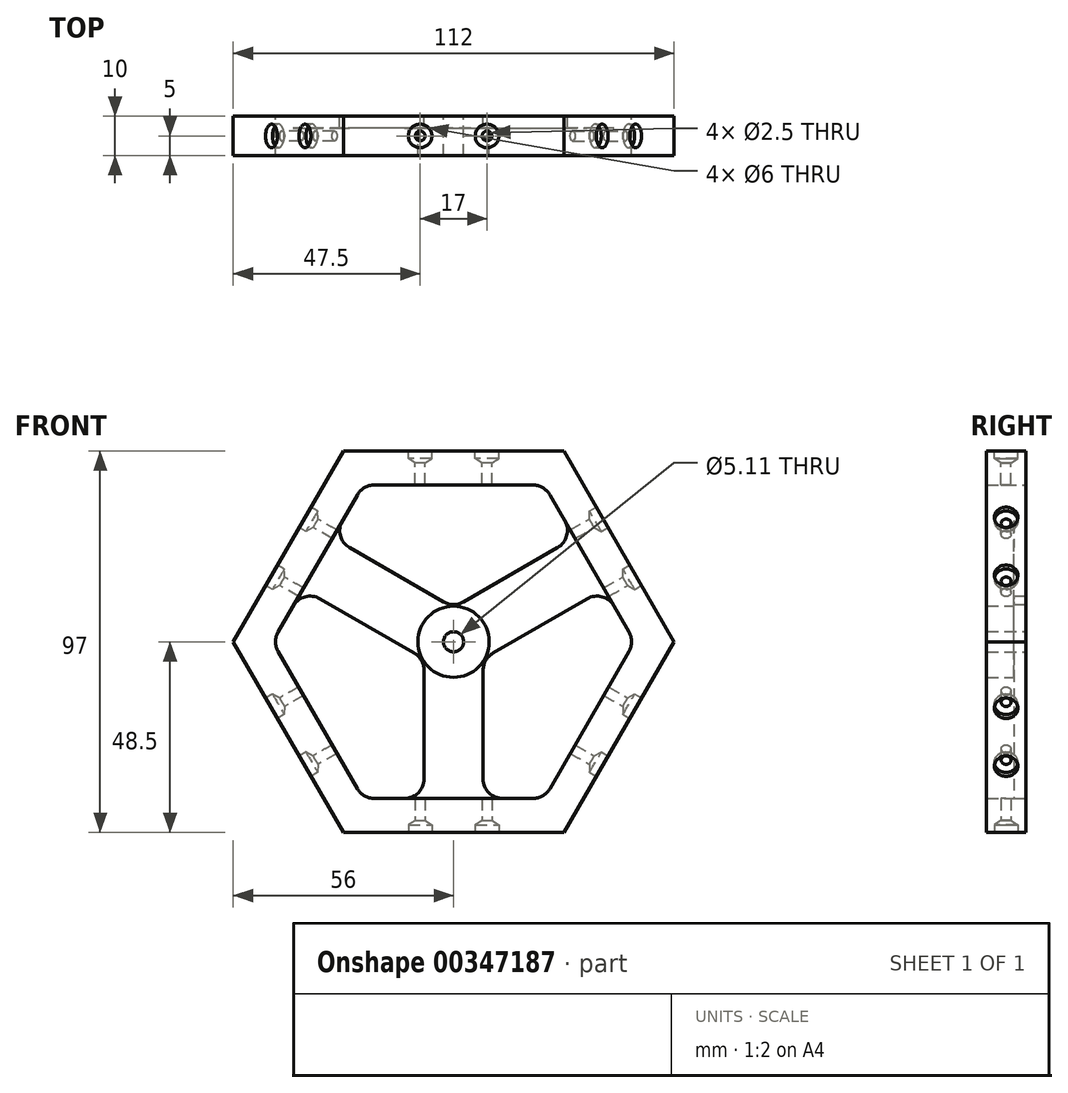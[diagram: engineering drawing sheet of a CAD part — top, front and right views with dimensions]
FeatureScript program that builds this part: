
annotation { "Feature Type Name" : "Feature", "Feature Type Description" : "" }
export const myFeature = defineFeature(function(context is Context, id is Id, definition is map)
    precondition{}
    {
        {
            var Q0;
            Q0=qCreatedBy(makeId("Front.planeOp"),FACE);
            var sketch = newSketch(context, id + "F0", { "sketchPlane" : qUnion([Q0])});
            skCircle(sketch, "E0.cCircle", {"center": v(0, 0) * mm, "radius": 56 * mm, "construction": true});
            skLineSegment(sketch, "E0.0", {"start": v(56, 0) * mm, "end": v(28, -48.5) * mm});
            skLineSegment(sketch, "E0.1", {"start": v(28, -48.5) * mm, "end": v(-28, -48.5) * mm});
            skLineSegment(sketch, "E0.2", {"start": v(-28, -48.5) * mm, "end": v(-56, 0) * mm});
            skLineSegment(sketch, "E0.3", {"start": v(-56, 0) * mm, "end": v(-28, 48.5) * mm});
            skLineSegment(sketch, "E0.4", {"start": v(-28, 48.5) * mm, "end": v(28, 48.5) * mm});
            skLineSegment(sketch, "E0.5", {"start": v(28, 48.5) * mm, "end": v(56, 0) * mm});
            skCircle(sketch, "E1.cCircle", {"center": v(0, 0) * mm, "radius": 46 * mm, "construction": true});
            skLineSegment(sketch, "E1.0", {"start": v(44.56, -2.5) * mm, "end": v(24.44, -37.34) * mm});
            skLineSegment(sketch, "E1.1", {"start": v(20.11, -39.84) * mm, "end": v(12.5, -39.84) * mm});
            skLineSegment(sketch, "E1.2", {"start": v(-24.44, -37.34) * mm, "end": v(-44.56, -2.5) * mm});
            skLineSegment(sketch, "E1.3", {"start": v(-28.25, 30.74) * mm, "end": v(-24.44, 37.34) * mm});
            skLineSegment(sketch, "E1.4", {"start": v(-20.11, 39.84) * mm, "end": v(20.11, 39.84) * mm});
            skLineSegment(sketch, "E1.5", {"start": v(24.44, 37.34) * mm, "end": v(28.25, 30.74) * mm});
            skLineSegment(sketch, "E2", {"start": v(7.5, -7.22) * mm, "end": v(7.5, -34.84) * mm});
            skLineSegment(sketch, "E3", {"start": v(-7.5, -7.22) * mm, "end": v(-7.5, -34.84) * mm});
            skLineSegment(sketch, "E4", {"start": v(10, -2.89) * mm, "end": v(33.92, 10.92) * mm});
            skLineSegment(sketch, "E5", {"start": v(2.5, 10.1) * mm, "end": v(26.42, 23.91) * mm});
            skLineSegment(sketch, "E6", {"start": v(-2.5, 10.1) * mm, "end": v(-26.42, 23.91) * mm});
            skLineSegment(sketch, "E7", {"start": v(-10, -2.89) * mm, "end": v(-33.92, 10.92) * mm});
            skPoint(sketch, "E8.newPointB", {"position": v(-46, 0) * mm});
            skArc(sketch, "E8.filletArc", {"start": v(-28.25, 30.74) * mm, "mid": v(-28.75, 26.95) * mm, "end": v(-26.42, 23.91) * mm});
            skPoint(sketch, "E9.visualSharp", {"position": v(-23, 39.84) * mm});
            skArc(sketch, "E9.filletArc", {"start": v(-20.11, 39.84) * mm, "mid": v(-22.61, 39.17) * mm, "end": v(-24.44, 37.34) * mm});
            skPoint(sketch, "E10.visualSharp", {"position": v(23, 39.84) * mm});
            skArc(sketch, "E10.filletArc", {"start": v(24.44, 37.34) * mm, "mid": v(22.61, 39.17) * mm, "end": v(20.11, 39.84) * mm});
            skPoint(sketch, "E11.newPointA", {"position": v(46, 0) * mm});
            skArc(sketch, "E11.filletArc", {"start": v(26.42, 23.91) * mm, "mid": v(28.75, 26.95) * mm, "end": v(28.25, 30.74) * mm});
            skPoint(sketch, "E12.visualSharp", {"position": v(23, -39.84) * mm});
            skArc(sketch, "E12.filletArc", {"start": v(20.11, -39.84) * mm, "mid": v(22.61, -39.17) * mm, "end": v(24.44, -37.34) * mm});
            skArc(sketch, "E13.filletArc", {"start": v(7.5, -34.84) * mm, "mid": v(8.96, -38.37) * mm, "end": v(12.5, -39.84) * mm});
            skArc(sketch, "E14.filletArc", {"start": v(10, -2.89) * mm, "mid": v(8.17, -4.72) * mm, "end": v(7.5, -7.22) * mm});
            skArc(sketch, "E15.filletArc", {"start": v(-7.5, -7.22) * mm, "mid": v(-8.17, -4.72) * mm, "end": v(-10, -2.89) * mm});
            skArc(sketch, "E16.filletArc", {"start": v(-2.5, 10.1) * mm, "mid": v(0, 9.43) * mm, "end": v(2.5, 10.1) * mm});
            skLineSegment(sketch, "E17", {"start": v(-40.75, 9.1) * mm, "end": v(-44.56, 2.5) * mm});
            skLineSegment(sketch, "E18", {"start": v(-20.11, -39.84) * mm, "end": v(-12.5, -39.84) * mm});
            skLineSegment(sketch, "E19", {"start": v(44.56, 2.5) * mm, "end": v(40.75, 9.1) * mm});
            skPoint(sketch, "E20.visualSharp", {"position": v(38.25, 13.42) * mm});
            skArc(sketch, "E20.filletArc", {"start": v(40.75, 9.1) * mm, "mid": v(37.71, 11.42) * mm, "end": v(33.92, 10.92) * mm});
            skArc(sketch, "E21.filletArc", {"start": v(44.56, -2.5) * mm, "mid": v(45.23, 0) * mm, "end": v(44.56, 2.5) * mm});
            skPoint(sketch, "E22.visualSharp", {"position": v(-38.25, 13.42) * mm});
            skArc(sketch, "E22.filletArc", {"start": v(-33.92, 10.92) * mm, "mid": v(-37.71, 11.42) * mm, "end": v(-40.75, 9.1) * mm});
            skPoint(sketch, "E23.visualSharp", {"position": v(-7.5, -39.84) * mm});
            skArc(sketch, "E23.filletArc", {"start": v(-12.5, -39.84) * mm, "mid": v(-8.96, -38.37) * mm, "end": v(-7.5, -34.84) * mm});
            skPoint(sketch, "E24.visualSharp", {"position": v(-23, -39.84) * mm});
            skArc(sketch, "E24.filletArc", {"start": v(-24.44, -37.34) * mm, "mid": v(-22.61, -39.17) * mm, "end": v(-20.11, -39.84) * mm});
            skArc(sketch, "E25.filletArc", {"start": v(-44.56, 2.5) * mm, "mid": v(-45.23, 0) * mm, "end": v(-44.56, -2.5) * mm});
            skCircle(sketch, "E26", {"center": v(0, 0) * mm, "radius": 9.05 * mm});
            skLineSegment(sketch, "E27", {"start": v(-28.25, 30.74) * mm, "end": v(-40.75, 9.1) * mm});
            skLineSegment(sketch, "E28", {"start": v(28.25, 30.74) * mm, "end": v(40.75, 9.1) * mm});
            skLineSegment(sketch, "E29", {"start": v(12.5, -39.84) * mm, "end": v(-12.5, -39.84) * mm});
            skSolve(sketch);
        }
        {
            var Q0;
            Q0=makeQuery(id+"F0.imprint","IMPRINT",FACE,{"disambiguationData":[TD([[makeQuery(id+"F0.imprint","IMPRINT",EDGE,{"derivedFrom":sQuery(id+"F0.wireOp",EDGE,"E0.0")}),-1.0]])]});
            var Q1;
            Q1=makeQuery(id+"F0.imprint","IMPRINT",FACE,{"disambiguationData":[TD([[makeQuery(id+"F0.imprint","IMPRINT",EDGE,{"derivedFrom":sQuery(id+"F0.wireOp",EDGE,"E26")}),1.0]])]});
            var Q2;
            Q2=makeQuery(id+"F0.imprint","IMPRINT",FACE,{"disambiguationData":[TD([[makeQuery(id+"F0.imprint","IMPRINT",EDGE,{"derivedFrom":sQuery(id+"F0.wireOp",EDGE,"E2")}),-1.0]])]});
            extrude(context, id + "F1", {"entities" : qUnion([Q0, Q1, Q2]), "depth" : 3 * mm});
        }
        {
            var Q0;
            Q0 = qSketchRegion(id + "F0", true);
            var Q1;
            Q1=makeQuery(id+"F0.imprint","IMPRINT",FACE,{"disambiguationData":[TD([[makeQuery(id+"F0.imprint","IMPRINT",EDGE,{"derivedFrom":sQuery(id+"F0.wireOp",EDGE,"E26")}),1.0]])]});
            extrude(context, id + "F2", {"entities" : qUnion([Q0, Q1]), "operationType" : NewBodyOperationType.ADD, "depth" : 10 * mm});
        }
        {
            var Q0;
            {var subQ0=sQuery(id+"F0.wireOp",EDGE,"E0.1");Q0=makeQuery(id+"F2.boolean.opBoolean","MERGE",FACE,{"derivedFrom":[makeQuery(id+"F1.opExtrude","SWEPT_FACE",FACE,{"disambiguationData":[OSD([subQ0])]}),makeQuery(id+"F2.opExtrude","SWEPT_FACE",FACE,{"disambiguationData":[OSD([subQ0])]})]});}
            var sketch = newSketch(context, id + "F3", { "sketchPlane" : qUnion([Q0])});
            skPoint(sketch, "E30", {"position": v(-8.5, 5) * mm});
            skPoint(sketch, "E31", {"position": v(8.5, 5) * mm});
            skSolve(sketch);
        }
        {
            var Q0;
            {var subQ0=sQuery(id+"F0.wireOp",EDGE,"E0.0");Q0=makeQuery(id+"F2.boolean.opBoolean","MERGE",FACE,{"derivedFrom":[makeQuery(id+"F1.opExtrude","SWEPT_FACE",FACE,{"disambiguationData":[OSD([subQ0])]}),makeQuery(id+"F2.opExtrude","SWEPT_FACE",FACE,{"disambiguationData":[OSD([subQ0])]})]});}
            var sketch = newSketch(context, id + "F4", { "sketchPlane" : qUnion([Q0])});
            skPoint(sketch, "E32", {"position": v(-5, -8.5) * mm});
            skPoint(sketch, "E33", {"position": v(-5, 8.5) * mm});
            skSolve(sketch);
        }
        {
            var Q0;
            {var subQ0=sQuery(id+"F0.wireOp",EDGE,"E0.5");Q0=makeQuery(id+"F2.boolean.opBoolean","MERGE",FACE,{"derivedFrom":[makeQuery(id+"F1.opExtrude","SWEPT_FACE",FACE,{"disambiguationData":[OSD([subQ0])]}),makeQuery(id+"F2.opExtrude","SWEPT_FACE",FACE,{"disambiguationData":[OSD([subQ0])]})]});}
            var sketch = newSketch(context, id + "F5", { "sketchPlane" : qUnion([Q0])});
            skPoint(sketch, "E34", {"position": v(-5, -8.5) * mm});
            skPoint(sketch, "E35", {"position": v(-5, 8.5) * mm});
            skSolve(sketch);
        }
        {
            var Q0;
            {var subQ0=sQuery(id+"F0.wireOp",EDGE,"E0.3");Q0=makeQuery(id+"F2.boolean.opBoolean","MERGE",FACE,{"derivedFrom":[makeQuery(id+"F1.opExtrude","SWEPT_FACE",FACE,{"disambiguationData":[OSD([subQ0])]}),makeQuery(id+"F2.opExtrude","SWEPT_FACE",FACE,{"disambiguationData":[OSD([subQ0])]})]});}
            var sketch = newSketch(context, id + "F6", { "sketchPlane" : qUnion([Q0])});
            skPoint(sketch, "E36.endSnap0", {"position": v(5, 28) * mm});
            skPoint(sketch, "E37", {"position": v(5, 8.5) * mm});
            skPoint(sketch, "E38", {"position": v(5, -8.5) * mm});
            skSolve(sketch);
        }
        {
            var Q0;
            {var subQ0=sQuery(id+"F0.wireOp",EDGE,"E0.2");Q0=makeQuery(id+"F2.boolean.opBoolean","MERGE",FACE,{"derivedFrom":[makeQuery(id+"F1.opExtrude","SWEPT_FACE",FACE,{"disambiguationData":[OSD([subQ0])]}),makeQuery(id+"F2.opExtrude","SWEPT_FACE",FACE,{"disambiguationData":[OSD([subQ0])]})]});}
            var sketch = newSketch(context, id + "F7", { "sketchPlane" : qUnion([Q0])});
            skPoint(sketch, "E39", {"position": v(5, 8.5) * mm});
            skPoint(sketch, "E40", {"position": v(5, -8.5) * mm});
            skSolve(sketch);
        }
        {
            var Q0;
            Q0=sQuery(id+"F3.wireOp",VERTEX,"E30");
            var Q1;
            Q1=sQuery(id+"F3.wireOp",VERTEX,"E31");
            var Q2;
            Q2=makeQuery(id+"F1.opExtrude","SWEPT_BODY",BODY,{"disambiguationData":[OSD([sQuery(id+"F0.wireOp",EDGE,"E0.0"),sQuery(id+"F0.wireOp",EDGE,"E0.1"),sQuery(id+"F0.wireOp",EDGE,"E0.2"),sQuery(id+"F0.wireOp",EDGE,"E0.3"),sQuery(id+"F0.wireOp",EDGE,"E0.4"),sQuery(id+"F0.wireOp",EDGE,"E0.5"),sQuery(id+"F0.wireOp",EDGE,"E1.0"),sQuery(id+"F0.wireOp",EDGE,"E1.1"),sQuery(id+"F0.wireOp",EDGE,"E1.2"),sQuery(id+"F0.wireOp",EDGE,"E1.3"),sQuery(id+"F0.wireOp",EDGE,"E1.4"),sQuery(id+"F0.wireOp",EDGE,"E1.5"),sQuery(id+"F0.wireOp",EDGE,"E2"),sQuery(id+"F0.wireOp",EDGE,"E3"),sQuery(id+"F0.wireOp",EDGE,"E4"),sQuery(id+"F0.wireOp",EDGE,"E5"),sQuery(id+"F0.wireOp",EDGE,"E6"),sQuery(id+"F0.wireOp",EDGE,"E7"),sQuery(id+"F0.wireOp",EDGE,"E8.filletArc"),sQuery(id+"F0.wireOp",EDGE,"E9.filletArc"),sQuery(id+"F0.wireOp",EDGE,"E10.filletArc"),sQuery(id+"F0.wireOp",EDGE,"E11.filletArc"),sQuery(id+"F0.wireOp",EDGE,"E12.filletArc"),sQuery(id+"F0.wireOp",EDGE,"E13.filletArc"),sQuery(id+"F0.wireOp",EDGE,"E14.filletArc"),sQuery(id+"F0.wireOp",EDGE,"E15.filletArc"),sQuery(id+"F0.wireOp",EDGE,"E16.filletArc"),sQuery(id+"F0.wireOp",EDGE,"E17"),sQuery(id+"F0.wireOp",EDGE,"E18"),sQuery(id+"F0.wireOp",EDGE,"E19"),sQuery(id+"F0.wireOp",EDGE,"E20.filletArc"),sQuery(id+"F0.wireOp",EDGE,"E21.filletArc"),sQuery(id+"F0.wireOp",EDGE,"E22.filletArc"),sQuery(id+"F0.wireOp",EDGE,"E23.filletArc"),sQuery(id+"F0.wireOp",EDGE,"E24.filletArc"),sQuery(id+"F0.wireOp",EDGE,"E25.filletArc")])]});
            hole(context, id + "F8", {"style" : HoleStyle.SIMPLE, "endStyle" : HoleEndStyle.BLIND, "holeDiameter" : 6 * mm, "holeDepth" : 2 * mm, "tappedDepth" : 12 * mm, "tapClearance" : 3, "locations" : qUnion([Q0, Q1]), "scope" : qUnion([Q2])});
        }
        {
            var Q0;
            Q0=sQuery(id+"F3.wireOp",VERTEX,"E30");
            var Q1;
            Q1=sQuery(id+"F3.wireOp",VERTEX,"E31");
            var Q2;
            Q2=makeQuery(id+"F1.opExtrude","SWEPT_BODY",BODY,{"disambiguationData":[OSD([sQuery(id+"F0.wireOp",EDGE,"E0.0"),sQuery(id+"F0.wireOp",EDGE,"E0.1"),sQuery(id+"F0.wireOp",EDGE,"E0.2"),sQuery(id+"F0.wireOp",EDGE,"E0.3"),sQuery(id+"F0.wireOp",EDGE,"E0.4"),sQuery(id+"F0.wireOp",EDGE,"E0.5"),sQuery(id+"F0.wireOp",EDGE,"E1.0"),sQuery(id+"F0.wireOp",EDGE,"E1.1"),sQuery(id+"F0.wireOp",EDGE,"E1.2"),sQuery(id+"F0.wireOp",EDGE,"E1.3"),sQuery(id+"F0.wireOp",EDGE,"E1.4"),sQuery(id+"F0.wireOp",EDGE,"E1.5"),sQuery(id+"F0.wireOp",EDGE,"E2"),sQuery(id+"F0.wireOp",EDGE,"E3"),sQuery(id+"F0.wireOp",EDGE,"E4"),sQuery(id+"F0.wireOp",EDGE,"E5"),sQuery(id+"F0.wireOp",EDGE,"E6"),sQuery(id+"F0.wireOp",EDGE,"E7"),sQuery(id+"F0.wireOp",EDGE,"E8.filletArc"),sQuery(id+"F0.wireOp",EDGE,"E9.filletArc"),sQuery(id+"F0.wireOp",EDGE,"E10.filletArc"),sQuery(id+"F0.wireOp",EDGE,"E11.filletArc"),sQuery(id+"F0.wireOp",EDGE,"E12.filletArc"),sQuery(id+"F0.wireOp",EDGE,"E13.filletArc"),sQuery(id+"F0.wireOp",EDGE,"E14.filletArc"),sQuery(id+"F0.wireOp",EDGE,"E15.filletArc"),sQuery(id+"F0.wireOp",EDGE,"E16.filletArc"),sQuery(id+"F0.wireOp",EDGE,"E17"),sQuery(id+"F0.wireOp",EDGE,"E18"),sQuery(id+"F0.wireOp",EDGE,"E19"),sQuery(id+"F0.wireOp",EDGE,"E20.filletArc"),sQuery(id+"F0.wireOp",EDGE,"E21.filletArc"),sQuery(id+"F0.wireOp",EDGE,"E22.filletArc"),sQuery(id+"F0.wireOp",EDGE,"E23.filletArc"),sQuery(id+"F0.wireOp",EDGE,"E24.filletArc"),sQuery(id+"F0.wireOp",EDGE,"E25.filletArc")])]});
            hole(context, id + "F9", {"style" : HoleStyle.SIMPLE, "endStyle" : HoleEndStyle.BLIND, "standardTappedOrClearance" : lookupTablePath({ "standard" : "ISO", "engagement" : "75%", "pitch" : "0.5 mm", "size" : "M3", "type" : "Tapped" }), "standardBlindInLast" : lookupTablePath({ "standard" : "ISO", "engagement" : "75%", "pitch" : "0.5 mm", "size" : "M3", "type" : "Tapped" }), "holeDiameter" : 2.5 * mm, "showTappedDepth" : true, "holeDepth" : 13.5 * mm, "tappedDepth" : 12 * mm, "tapClearance" : 3, "locations" : qUnion([Q0, Q1]), "scope" : qUnion([Q2]), "majorDiameter" : 3 * mm});
        }
        {
            var Q0;
            Q0=sQuery(id+"F4.wireOp",VERTEX,"E32");
            var Q1;
            Q1=sQuery(id+"F4.wireOp",VERTEX,"E33");
            var Q2;
            Q2=makeQuery(id+"F1.opExtrude","SWEPT_BODY",BODY,{"disambiguationData":[OSD([sQuery(id+"F0.wireOp",EDGE,"E0.0"),sQuery(id+"F0.wireOp",EDGE,"E0.1"),sQuery(id+"F0.wireOp",EDGE,"E0.2"),sQuery(id+"F0.wireOp",EDGE,"E0.3"),sQuery(id+"F0.wireOp",EDGE,"E0.4"),sQuery(id+"F0.wireOp",EDGE,"E0.5"),sQuery(id+"F0.wireOp",EDGE,"E1.0"),sQuery(id+"F0.wireOp",EDGE,"E1.1"),sQuery(id+"F0.wireOp",EDGE,"E1.2"),sQuery(id+"F0.wireOp",EDGE,"E1.3"),sQuery(id+"F0.wireOp",EDGE,"E1.4"),sQuery(id+"F0.wireOp",EDGE,"E1.5"),sQuery(id+"F0.wireOp",EDGE,"E2"),sQuery(id+"F0.wireOp",EDGE,"E3"),sQuery(id+"F0.wireOp",EDGE,"E4"),sQuery(id+"F0.wireOp",EDGE,"E5"),sQuery(id+"F0.wireOp",EDGE,"E6"),sQuery(id+"F0.wireOp",EDGE,"E7"),sQuery(id+"F0.wireOp",EDGE,"E8.filletArc"),sQuery(id+"F0.wireOp",EDGE,"E9.filletArc"),sQuery(id+"F0.wireOp",EDGE,"E10.filletArc"),sQuery(id+"F0.wireOp",EDGE,"E11.filletArc"),sQuery(id+"F0.wireOp",EDGE,"E12.filletArc"),sQuery(id+"F0.wireOp",EDGE,"E13.filletArc"),sQuery(id+"F0.wireOp",EDGE,"E14.filletArc"),sQuery(id+"F0.wireOp",EDGE,"E15.filletArc"),sQuery(id+"F0.wireOp",EDGE,"E16.filletArc"),sQuery(id+"F0.wireOp",EDGE,"E17"),sQuery(id+"F0.wireOp",EDGE,"E18"),sQuery(id+"F0.wireOp",EDGE,"E19"),sQuery(id+"F0.wireOp",EDGE,"E20.filletArc"),sQuery(id+"F0.wireOp",EDGE,"E21.filletArc"),sQuery(id+"F0.wireOp",EDGE,"E22.filletArc"),sQuery(id+"F0.wireOp",EDGE,"E23.filletArc"),sQuery(id+"F0.wireOp",EDGE,"E24.filletArc"),sQuery(id+"F0.wireOp",EDGE,"E25.filletArc")])]});
            hole(context, id + "F10", {"style" : HoleStyle.SIMPLE, "endStyle" : HoleEndStyle.BLIND, "standardTappedOrClearance" : lookupTablePath({ "standard" : "ISO", "engagement" : "75%", "pitch" : "0.5 mm", "size" : "M3", "type" : "Tapped" }), "standardBlindInLast" : lookupTablePath({ "standard" : "ISO", "engagement" : "75%", "pitch" : "0.5 mm", "size" : "M3", "type" : "Tapped" }), "holeDiameter" : 2.5 * mm, "showTappedDepth" : true, "holeDepth" : 13.5 * mm, "tappedDepth" : 12 * mm, "tapClearance" : 3, "locations" : qUnion([Q0, Q1]), "scope" : qUnion([Q2]), "majorDiameter" : 3 * mm});
        }
        {
            var Q0;
            Q0=sQuery(id+"F4.wireOp",VERTEX,"E32");
            var Q1;
            Q1=sQuery(id+"F4.wireOp",VERTEX,"E33");
            var Q2;
            Q2=makeQuery(id+"F1.opExtrude","SWEPT_BODY",BODY,{"disambiguationData":[OSD([sQuery(id+"F0.wireOp",EDGE,"E0.0"),sQuery(id+"F0.wireOp",EDGE,"E0.1"),sQuery(id+"F0.wireOp",EDGE,"E0.2"),sQuery(id+"F0.wireOp",EDGE,"E0.3"),sQuery(id+"F0.wireOp",EDGE,"E0.4"),sQuery(id+"F0.wireOp",EDGE,"E0.5"),sQuery(id+"F0.wireOp",EDGE,"E1.0"),sQuery(id+"F0.wireOp",EDGE,"E1.1"),sQuery(id+"F0.wireOp",EDGE,"E1.2"),sQuery(id+"F0.wireOp",EDGE,"E1.3"),sQuery(id+"F0.wireOp",EDGE,"E1.4"),sQuery(id+"F0.wireOp",EDGE,"E1.5"),sQuery(id+"F0.wireOp",EDGE,"E2"),sQuery(id+"F0.wireOp",EDGE,"E3"),sQuery(id+"F0.wireOp",EDGE,"E4"),sQuery(id+"F0.wireOp",EDGE,"E5"),sQuery(id+"F0.wireOp",EDGE,"E6"),sQuery(id+"F0.wireOp",EDGE,"E7"),sQuery(id+"F0.wireOp",EDGE,"E8.filletArc"),sQuery(id+"F0.wireOp",EDGE,"E9.filletArc"),sQuery(id+"F0.wireOp",EDGE,"E10.filletArc"),sQuery(id+"F0.wireOp",EDGE,"E11.filletArc"),sQuery(id+"F0.wireOp",EDGE,"E12.filletArc"),sQuery(id+"F0.wireOp",EDGE,"E13.filletArc"),sQuery(id+"F0.wireOp",EDGE,"E14.filletArc"),sQuery(id+"F0.wireOp",EDGE,"E15.filletArc"),sQuery(id+"F0.wireOp",EDGE,"E16.filletArc"),sQuery(id+"F0.wireOp",EDGE,"E17"),sQuery(id+"F0.wireOp",EDGE,"E18"),sQuery(id+"F0.wireOp",EDGE,"E19"),sQuery(id+"F0.wireOp",EDGE,"E20.filletArc"),sQuery(id+"F0.wireOp",EDGE,"E21.filletArc"),sQuery(id+"F0.wireOp",EDGE,"E22.filletArc"),sQuery(id+"F0.wireOp",EDGE,"E23.filletArc"),sQuery(id+"F0.wireOp",EDGE,"E24.filletArc"),sQuery(id+"F0.wireOp",EDGE,"E25.filletArc")])]});
            hole(context, id + "F11", {"style" : HoleStyle.SIMPLE, "endStyle" : HoleEndStyle.BLIND, "holeDiameter" : 6 * mm, "holeDepth" : 2 * mm, "tappedDepth" : 12 * mm, "tapClearance" : 3, "locations" : qUnion([Q0, Q1]), "scope" : qUnion([Q2])});
        }
        {
            var Q0;
            Q0=sQuery(id+"F5.wireOp",VERTEX,"E34");
            var Q1;
            Q1=sQuery(id+"F5.wireOp",VERTEX,"E35");
            var Q2;
            Q2=makeQuery(id+"F1.opExtrude","SWEPT_BODY",BODY,{"disambiguationData":[OSD([sQuery(id+"F0.wireOp",EDGE,"E0.0"),sQuery(id+"F0.wireOp",EDGE,"E0.1"),sQuery(id+"F0.wireOp",EDGE,"E0.2"),sQuery(id+"F0.wireOp",EDGE,"E0.3"),sQuery(id+"F0.wireOp",EDGE,"E0.4"),sQuery(id+"F0.wireOp",EDGE,"E0.5"),sQuery(id+"F0.wireOp",EDGE,"E1.0"),sQuery(id+"F0.wireOp",EDGE,"E1.1"),sQuery(id+"F0.wireOp",EDGE,"E1.2"),sQuery(id+"F0.wireOp",EDGE,"E1.3"),sQuery(id+"F0.wireOp",EDGE,"E1.4"),sQuery(id+"F0.wireOp",EDGE,"E1.5"),sQuery(id+"F0.wireOp",EDGE,"E2"),sQuery(id+"F0.wireOp",EDGE,"E3"),sQuery(id+"F0.wireOp",EDGE,"E4"),sQuery(id+"F0.wireOp",EDGE,"E5"),sQuery(id+"F0.wireOp",EDGE,"E6"),sQuery(id+"F0.wireOp",EDGE,"E7"),sQuery(id+"F0.wireOp",EDGE,"E8.filletArc"),sQuery(id+"F0.wireOp",EDGE,"E9.filletArc"),sQuery(id+"F0.wireOp",EDGE,"E10.filletArc"),sQuery(id+"F0.wireOp",EDGE,"E11.filletArc"),sQuery(id+"F0.wireOp",EDGE,"E12.filletArc"),sQuery(id+"F0.wireOp",EDGE,"E13.filletArc"),sQuery(id+"F0.wireOp",EDGE,"E14.filletArc"),sQuery(id+"F0.wireOp",EDGE,"E15.filletArc"),sQuery(id+"F0.wireOp",EDGE,"E16.filletArc"),sQuery(id+"F0.wireOp",EDGE,"E17"),sQuery(id+"F0.wireOp",EDGE,"E18"),sQuery(id+"F0.wireOp",EDGE,"E19"),sQuery(id+"F0.wireOp",EDGE,"E20.filletArc"),sQuery(id+"F0.wireOp",EDGE,"E21.filletArc"),sQuery(id+"F0.wireOp",EDGE,"E22.filletArc"),sQuery(id+"F0.wireOp",EDGE,"E23.filletArc"),sQuery(id+"F0.wireOp",EDGE,"E24.filletArc"),sQuery(id+"F0.wireOp",EDGE,"E25.filletArc")])]});
            hole(context, id + "F12", {"style" : HoleStyle.SIMPLE, "endStyle" : HoleEndStyle.BLIND, "holeDiameter" : 6 * mm, "holeDepth" : 2 * mm, "tappedDepth" : 12 * mm, "tapClearance" : 3, "locations" : qUnion([Q0, Q1]), "scope" : qUnion([Q2])});
        }
        {
            var Q0;
            Q0=sQuery(id+"F5.wireOp",VERTEX,"E34");
            var Q1;
            Q1=sQuery(id+"F5.wireOp",VERTEX,"E35");
            var Q2;
            Q2=makeQuery(id+"F1.opExtrude","SWEPT_BODY",BODY,{"disambiguationData":[OSD([sQuery(id+"F0.wireOp",EDGE,"E0.0"),sQuery(id+"F0.wireOp",EDGE,"E0.1"),sQuery(id+"F0.wireOp",EDGE,"E0.2"),sQuery(id+"F0.wireOp",EDGE,"E0.3"),sQuery(id+"F0.wireOp",EDGE,"E0.4"),sQuery(id+"F0.wireOp",EDGE,"E0.5"),sQuery(id+"F0.wireOp",EDGE,"E1.0"),sQuery(id+"F0.wireOp",EDGE,"E1.1"),sQuery(id+"F0.wireOp",EDGE,"E1.2"),sQuery(id+"F0.wireOp",EDGE,"E1.3"),sQuery(id+"F0.wireOp",EDGE,"E1.4"),sQuery(id+"F0.wireOp",EDGE,"E1.5"),sQuery(id+"F0.wireOp",EDGE,"E2"),sQuery(id+"F0.wireOp",EDGE,"E3"),sQuery(id+"F0.wireOp",EDGE,"E4"),sQuery(id+"F0.wireOp",EDGE,"E5"),sQuery(id+"F0.wireOp",EDGE,"E6"),sQuery(id+"F0.wireOp",EDGE,"E7"),sQuery(id+"F0.wireOp",EDGE,"E8.filletArc"),sQuery(id+"F0.wireOp",EDGE,"E9.filletArc"),sQuery(id+"F0.wireOp",EDGE,"E10.filletArc"),sQuery(id+"F0.wireOp",EDGE,"E11.filletArc"),sQuery(id+"F0.wireOp",EDGE,"E12.filletArc"),sQuery(id+"F0.wireOp",EDGE,"E13.filletArc"),sQuery(id+"F0.wireOp",EDGE,"E14.filletArc"),sQuery(id+"F0.wireOp",EDGE,"E15.filletArc"),sQuery(id+"F0.wireOp",EDGE,"E16.filletArc"),sQuery(id+"F0.wireOp",EDGE,"E17"),sQuery(id+"F0.wireOp",EDGE,"E18"),sQuery(id+"F0.wireOp",EDGE,"E19"),sQuery(id+"F0.wireOp",EDGE,"E20.filletArc"),sQuery(id+"F0.wireOp",EDGE,"E21.filletArc"),sQuery(id+"F0.wireOp",EDGE,"E22.filletArc"),sQuery(id+"F0.wireOp",EDGE,"E23.filletArc"),sQuery(id+"F0.wireOp",EDGE,"E24.filletArc"),sQuery(id+"F0.wireOp",EDGE,"E25.filletArc")])]});
            hole(context, id + "F13", {"style" : HoleStyle.SIMPLE, "endStyle" : HoleEndStyle.BLIND, "standardTappedOrClearance" : lookupTablePath({ "standard" : "ISO", "engagement" : "75%", "pitch" : "0.5 mm", "size" : "M3", "type" : "Tapped" }), "standardBlindInLast" : lookupTablePath({ "standard" : "ISO", "engagement" : "75%", "pitch" : "0.5 mm", "size" : "M3", "type" : "Tapped" }), "holeDiameter" : 2.5 * mm, "showTappedDepth" : true, "holeDepth" : 13.5 * mm, "tappedDepth" : 12 * mm, "tapClearance" : 3, "locations" : qUnion([Q0, Q1]), "scope" : qUnion([Q2]), "majorDiameter" : 3 * mm});
        }
        {
            var Q0;
            {var subQ0=sQuery(id+"F0.wireOp",EDGE,"E0.4");Q0=makeQuery(id+"F2.boolean.opBoolean","MERGE",FACE,{"derivedFrom":[makeQuery(id+"F1.opExtrude","SWEPT_FACE",FACE,{"disambiguationData":[OSD([subQ0])]}),makeQuery(id+"F2.opExtrude","SWEPT_FACE",FACE,{"disambiguationData":[OSD([subQ0])]})]});}
            var sketch = newSketch(context, id + "F14", { "sketchPlane" : qUnion([Q0])});
            skPoint(sketch, "E41", {"position": v(8.5, -5) * mm});
            skPoint(sketch, "E42", {"position": v(-8.5, -5) * mm});
            skSolve(sketch);
        }
        {
            var Q0;
            Q0=sQuery(id+"F14.wireOp",VERTEX,"E41");
            var Q1;
            Q1=sQuery(id+"F14.wireOp",VERTEX,"E42");
            var Q2;
            Q2=makeQuery(id+"F1.opExtrude","SWEPT_BODY",BODY,{"disambiguationData":[OSD([sQuery(id+"F0.wireOp",EDGE,"E0.0"),sQuery(id+"F0.wireOp",EDGE,"E0.1"),sQuery(id+"F0.wireOp",EDGE,"E0.2"),sQuery(id+"F0.wireOp",EDGE,"E0.3"),sQuery(id+"F0.wireOp",EDGE,"E0.4"),sQuery(id+"F0.wireOp",EDGE,"E0.5"),sQuery(id+"F0.wireOp",EDGE,"E1.0"),sQuery(id+"F0.wireOp",EDGE,"E1.1"),sQuery(id+"F0.wireOp",EDGE,"E1.2"),sQuery(id+"F0.wireOp",EDGE,"E1.3"),sQuery(id+"F0.wireOp",EDGE,"E1.4"),sQuery(id+"F0.wireOp",EDGE,"E1.5"),sQuery(id+"F0.wireOp",EDGE,"E2"),sQuery(id+"F0.wireOp",EDGE,"E3"),sQuery(id+"F0.wireOp",EDGE,"E4"),sQuery(id+"F0.wireOp",EDGE,"E5"),sQuery(id+"F0.wireOp",EDGE,"E6"),sQuery(id+"F0.wireOp",EDGE,"E7"),sQuery(id+"F0.wireOp",EDGE,"E8.filletArc"),sQuery(id+"F0.wireOp",EDGE,"E9.filletArc"),sQuery(id+"F0.wireOp",EDGE,"E10.filletArc"),sQuery(id+"F0.wireOp",EDGE,"E11.filletArc"),sQuery(id+"F0.wireOp",EDGE,"E12.filletArc"),sQuery(id+"F0.wireOp",EDGE,"E13.filletArc"),sQuery(id+"F0.wireOp",EDGE,"E14.filletArc"),sQuery(id+"F0.wireOp",EDGE,"E15.filletArc"),sQuery(id+"F0.wireOp",EDGE,"E16.filletArc"),sQuery(id+"F0.wireOp",EDGE,"E17"),sQuery(id+"F0.wireOp",EDGE,"E18"),sQuery(id+"F0.wireOp",EDGE,"E19"),sQuery(id+"F0.wireOp",EDGE,"E20.filletArc"),sQuery(id+"F0.wireOp",EDGE,"E21.filletArc"),sQuery(id+"F0.wireOp",EDGE,"E22.filletArc"),sQuery(id+"F0.wireOp",EDGE,"E23.filletArc"),sQuery(id+"F0.wireOp",EDGE,"E24.filletArc"),sQuery(id+"F0.wireOp",EDGE,"E25.filletArc")])]});
            hole(context, id + "F15", {"style" : HoleStyle.SIMPLE, "endStyle" : HoleEndStyle.BLIND, "standardTappedOrClearance" : lookupTablePath({ "standard" : "ISO", "engagement" : "75%", "pitch" : "0.5 mm", "size" : "M3", "type" : "Tapped" }), "standardBlindInLast" : lookupTablePath({ "standard" : "ISO", "engagement" : "75%", "pitch" : "0.5 mm", "size" : "M3", "type" : "Tapped" }), "holeDiameter" : 2.5 * mm, "showTappedDepth" : true, "holeDepth" : 13.5 * mm, "tappedDepth" : 12 * mm, "tapClearance" : 3, "locations" : qUnion([Q0, Q1]), "scope" : qUnion([Q2]), "majorDiameter" : 3 * mm});
        }
        {
            var Q0;
            Q0=sQuery(id+"F14.wireOp",VERTEX,"E41");
            var Q1;
            Q1=sQuery(id+"F14.wireOp",VERTEX,"E42");
            var Q2;
            Q2=makeQuery(id+"F1.opExtrude","SWEPT_BODY",BODY,{"disambiguationData":[OSD([sQuery(id+"F0.wireOp",EDGE,"E0.0"),sQuery(id+"F0.wireOp",EDGE,"E0.1"),sQuery(id+"F0.wireOp",EDGE,"E0.2"),sQuery(id+"F0.wireOp",EDGE,"E0.3"),sQuery(id+"F0.wireOp",EDGE,"E0.4"),sQuery(id+"F0.wireOp",EDGE,"E0.5"),sQuery(id+"F0.wireOp",EDGE,"E1.0"),sQuery(id+"F0.wireOp",EDGE,"E1.1"),sQuery(id+"F0.wireOp",EDGE,"E1.2"),sQuery(id+"F0.wireOp",EDGE,"E1.3"),sQuery(id+"F0.wireOp",EDGE,"E1.4"),sQuery(id+"F0.wireOp",EDGE,"E1.5"),sQuery(id+"F0.wireOp",EDGE,"E2"),sQuery(id+"F0.wireOp",EDGE,"E3"),sQuery(id+"F0.wireOp",EDGE,"E4"),sQuery(id+"F0.wireOp",EDGE,"E5"),sQuery(id+"F0.wireOp",EDGE,"E6"),sQuery(id+"F0.wireOp",EDGE,"E7"),sQuery(id+"F0.wireOp",EDGE,"E8.filletArc"),sQuery(id+"F0.wireOp",EDGE,"E9.filletArc"),sQuery(id+"F0.wireOp",EDGE,"E10.filletArc"),sQuery(id+"F0.wireOp",EDGE,"E11.filletArc"),sQuery(id+"F0.wireOp",EDGE,"E12.filletArc"),sQuery(id+"F0.wireOp",EDGE,"E13.filletArc"),sQuery(id+"F0.wireOp",EDGE,"E14.filletArc"),sQuery(id+"F0.wireOp",EDGE,"E15.filletArc"),sQuery(id+"F0.wireOp",EDGE,"E16.filletArc"),sQuery(id+"F0.wireOp",EDGE,"E17"),sQuery(id+"F0.wireOp",EDGE,"E18"),sQuery(id+"F0.wireOp",EDGE,"E19"),sQuery(id+"F0.wireOp",EDGE,"E20.filletArc"),sQuery(id+"F0.wireOp",EDGE,"E21.filletArc"),sQuery(id+"F0.wireOp",EDGE,"E22.filletArc"),sQuery(id+"F0.wireOp",EDGE,"E23.filletArc"),sQuery(id+"F0.wireOp",EDGE,"E24.filletArc"),sQuery(id+"F0.wireOp",EDGE,"E25.filletArc")])]});
            hole(context, id + "F16", {"style" : HoleStyle.SIMPLE, "endStyle" : HoleEndStyle.BLIND, "holeDiameter" : 6 * mm, "holeDepth" : 2 * mm, "tappedDepth" : 12 * mm, "tapClearance" : 3, "locations" : qUnion([Q0, Q1]), "scope" : qUnion([Q2])});
        }
        {
            var Q0;
            Q0=sQuery(id+"F6.wireOp",VERTEX,"E37");
            var Q1;
            Q1=sQuery(id+"F6.wireOp",VERTEX,"E38");
            var Q2;
            Q2=makeQuery(id+"F1.opExtrude","SWEPT_BODY",BODY,{"disambiguationData":[OSD([sQuery(id+"F0.wireOp",EDGE,"E0.0"),sQuery(id+"F0.wireOp",EDGE,"E0.1"),sQuery(id+"F0.wireOp",EDGE,"E0.2"),sQuery(id+"F0.wireOp",EDGE,"E0.3"),sQuery(id+"F0.wireOp",EDGE,"E0.4"),sQuery(id+"F0.wireOp",EDGE,"E0.5"),sQuery(id+"F0.wireOp",EDGE,"E1.0"),sQuery(id+"F0.wireOp",EDGE,"E1.1"),sQuery(id+"F0.wireOp",EDGE,"E1.2"),sQuery(id+"F0.wireOp",EDGE,"E1.3"),sQuery(id+"F0.wireOp",EDGE,"E1.4"),sQuery(id+"F0.wireOp",EDGE,"E1.5"),sQuery(id+"F0.wireOp",EDGE,"E2"),sQuery(id+"F0.wireOp",EDGE,"E3"),sQuery(id+"F0.wireOp",EDGE,"E4"),sQuery(id+"F0.wireOp",EDGE,"E5"),sQuery(id+"F0.wireOp",EDGE,"E6"),sQuery(id+"F0.wireOp",EDGE,"E7"),sQuery(id+"F0.wireOp",EDGE,"E8.filletArc"),sQuery(id+"F0.wireOp",EDGE,"E9.filletArc"),sQuery(id+"F0.wireOp",EDGE,"E10.filletArc"),sQuery(id+"F0.wireOp",EDGE,"E11.filletArc"),sQuery(id+"F0.wireOp",EDGE,"E12.filletArc"),sQuery(id+"F0.wireOp",EDGE,"E13.filletArc"),sQuery(id+"F0.wireOp",EDGE,"E14.filletArc"),sQuery(id+"F0.wireOp",EDGE,"E15.filletArc"),sQuery(id+"F0.wireOp",EDGE,"E16.filletArc"),sQuery(id+"F0.wireOp",EDGE,"E17"),sQuery(id+"F0.wireOp",EDGE,"E18"),sQuery(id+"F0.wireOp",EDGE,"E19"),sQuery(id+"F0.wireOp",EDGE,"E20.filletArc"),sQuery(id+"F0.wireOp",EDGE,"E21.filletArc"),sQuery(id+"F0.wireOp",EDGE,"E22.filletArc"),sQuery(id+"F0.wireOp",EDGE,"E23.filletArc"),sQuery(id+"F0.wireOp",EDGE,"E24.filletArc"),sQuery(id+"F0.wireOp",EDGE,"E25.filletArc")])]});
            hole(context, id + "F17", {"style" : HoleStyle.SIMPLE, "endStyle" : HoleEndStyle.BLIND, "holeDiameter" : 6 * mm, "holeDepth" : 2 * mm, "tappedDepth" : 12 * mm, "tapClearance" : 3, "locations" : qUnion([Q0, Q1]), "scope" : qUnion([Q2])});
        }
        {
            var Q0;
            Q0=sQuery(id+"F6.wireOp",VERTEX,"E37");
            var Q1;
            Q1=sQuery(id+"F6.wireOp",VERTEX,"E38");
            var Q2;
            Q2=makeQuery(id+"F1.opExtrude","SWEPT_BODY",BODY,{"disambiguationData":[OSD([sQuery(id+"F0.wireOp",EDGE,"E0.0"),sQuery(id+"F0.wireOp",EDGE,"E0.1"),sQuery(id+"F0.wireOp",EDGE,"E0.2"),sQuery(id+"F0.wireOp",EDGE,"E0.3"),sQuery(id+"F0.wireOp",EDGE,"E0.4"),sQuery(id+"F0.wireOp",EDGE,"E0.5"),sQuery(id+"F0.wireOp",EDGE,"E1.0"),sQuery(id+"F0.wireOp",EDGE,"E1.1"),sQuery(id+"F0.wireOp",EDGE,"E1.2"),sQuery(id+"F0.wireOp",EDGE,"E1.3"),sQuery(id+"F0.wireOp",EDGE,"E1.4"),sQuery(id+"F0.wireOp",EDGE,"E1.5"),sQuery(id+"F0.wireOp",EDGE,"E2"),sQuery(id+"F0.wireOp",EDGE,"E3"),sQuery(id+"F0.wireOp",EDGE,"E4"),sQuery(id+"F0.wireOp",EDGE,"E5"),sQuery(id+"F0.wireOp",EDGE,"E6"),sQuery(id+"F0.wireOp",EDGE,"E7"),sQuery(id+"F0.wireOp",EDGE,"E8.filletArc"),sQuery(id+"F0.wireOp",EDGE,"E9.filletArc"),sQuery(id+"F0.wireOp",EDGE,"E10.filletArc"),sQuery(id+"F0.wireOp",EDGE,"E11.filletArc"),sQuery(id+"F0.wireOp",EDGE,"E12.filletArc"),sQuery(id+"F0.wireOp",EDGE,"E13.filletArc"),sQuery(id+"F0.wireOp",EDGE,"E14.filletArc"),sQuery(id+"F0.wireOp",EDGE,"E15.filletArc"),sQuery(id+"F0.wireOp",EDGE,"E16.filletArc"),sQuery(id+"F0.wireOp",EDGE,"E17"),sQuery(id+"F0.wireOp",EDGE,"E18"),sQuery(id+"F0.wireOp",EDGE,"E19"),sQuery(id+"F0.wireOp",EDGE,"E20.filletArc"),sQuery(id+"F0.wireOp",EDGE,"E21.filletArc"),sQuery(id+"F0.wireOp",EDGE,"E22.filletArc"),sQuery(id+"F0.wireOp",EDGE,"E23.filletArc"),sQuery(id+"F0.wireOp",EDGE,"E24.filletArc"),sQuery(id+"F0.wireOp",EDGE,"E25.filletArc")])]});
            hole(context, id + "F18", {"style" : HoleStyle.SIMPLE, "endStyle" : HoleEndStyle.BLIND, "standardTappedOrClearance" : lookupTablePath({ "standard" : "ISO", "engagement" : "75%", "pitch" : "0.5 mm", "size" : "M3", "type" : "Tapped" }), "standardBlindInLast" : lookupTablePath({ "standard" : "ISO", "engagement" : "75%", "pitch" : "0.5 mm", "size" : "M3", "type" : "Tapped" }), "holeDiameter" : 2.5 * mm, "showTappedDepth" : true, "holeDepth" : 13.5 * mm, "tappedDepth" : 12 * mm, "tapClearance" : 3, "locations" : qUnion([Q0, Q1]), "scope" : qUnion([Q2]), "majorDiameter" : 3 * mm});
        }
        {
            var Q0;
            Q0=sQuery(id+"F7.wireOp",VERTEX,"E39");
            var Q1;
            Q1=sQuery(id+"F7.wireOp",VERTEX,"E40");
            var Q2;
            Q2=makeQuery(id+"F1.opExtrude","SWEPT_BODY",BODY,{"disambiguationData":[OSD([sQuery(id+"F0.wireOp",EDGE,"E0.0"),sQuery(id+"F0.wireOp",EDGE,"E0.1"),sQuery(id+"F0.wireOp",EDGE,"E0.2"),sQuery(id+"F0.wireOp",EDGE,"E0.3"),sQuery(id+"F0.wireOp",EDGE,"E0.4"),sQuery(id+"F0.wireOp",EDGE,"E0.5"),sQuery(id+"F0.wireOp",EDGE,"E1.0"),sQuery(id+"F0.wireOp",EDGE,"E1.1"),sQuery(id+"F0.wireOp",EDGE,"E1.2"),sQuery(id+"F0.wireOp",EDGE,"E1.3"),sQuery(id+"F0.wireOp",EDGE,"E1.4"),sQuery(id+"F0.wireOp",EDGE,"E1.5"),sQuery(id+"F0.wireOp",EDGE,"E2"),sQuery(id+"F0.wireOp",EDGE,"E3"),sQuery(id+"F0.wireOp",EDGE,"E4"),sQuery(id+"F0.wireOp",EDGE,"E5"),sQuery(id+"F0.wireOp",EDGE,"E6"),sQuery(id+"F0.wireOp",EDGE,"E7"),sQuery(id+"F0.wireOp",EDGE,"E8.filletArc"),sQuery(id+"F0.wireOp",EDGE,"E9.filletArc"),sQuery(id+"F0.wireOp",EDGE,"E10.filletArc"),sQuery(id+"F0.wireOp",EDGE,"E11.filletArc"),sQuery(id+"F0.wireOp",EDGE,"E12.filletArc"),sQuery(id+"F0.wireOp",EDGE,"E13.filletArc"),sQuery(id+"F0.wireOp",EDGE,"E14.filletArc"),sQuery(id+"F0.wireOp",EDGE,"E15.filletArc"),sQuery(id+"F0.wireOp",EDGE,"E16.filletArc"),sQuery(id+"F0.wireOp",EDGE,"E17"),sQuery(id+"F0.wireOp",EDGE,"E18"),sQuery(id+"F0.wireOp",EDGE,"E19"),sQuery(id+"F0.wireOp",EDGE,"E20.filletArc"),sQuery(id+"F0.wireOp",EDGE,"E21.filletArc"),sQuery(id+"F0.wireOp",EDGE,"E22.filletArc"),sQuery(id+"F0.wireOp",EDGE,"E23.filletArc"),sQuery(id+"F0.wireOp",EDGE,"E24.filletArc"),sQuery(id+"F0.wireOp",EDGE,"E25.filletArc")])]});
            hole(context, id + "F19", {"style" : HoleStyle.SIMPLE, "endStyle" : HoleEndStyle.BLIND, "standardTappedOrClearance" : lookupTablePath({ "standard" : "ISO", "engagement" : "75%", "pitch" : "0.5 mm", "size" : "M3", "type" : "Tapped" }), "standardBlindInLast" : lookupTablePath({ "standard" : "ISO", "engagement" : "75%", "pitch" : "0.5 mm", "size" : "M3", "type" : "Tapped" }), "holeDiameter" : 2.5 * mm, "showTappedDepth" : true, "holeDepth" : 13.5 * mm, "tappedDepth" : 12 * mm, "tapClearance" : 3, "locations" : qUnion([Q0, Q1]), "scope" : qUnion([Q2]), "majorDiameter" : 3 * mm});
        }
        {
            var Q0;
            Q0=sQuery(id+"F7.wireOp",VERTEX,"E39");
            var Q1;
            Q1=sQuery(id+"F7.wireOp",VERTEX,"E40");
            var Q2;
            Q2=makeQuery(id+"F1.opExtrude","SWEPT_BODY",BODY,{"disambiguationData":[OSD([sQuery(id+"F0.wireOp",EDGE,"E0.0"),sQuery(id+"F0.wireOp",EDGE,"E0.1"),sQuery(id+"F0.wireOp",EDGE,"E0.2"),sQuery(id+"F0.wireOp",EDGE,"E0.3"),sQuery(id+"F0.wireOp",EDGE,"E0.4"),sQuery(id+"F0.wireOp",EDGE,"E0.5"),sQuery(id+"F0.wireOp",EDGE,"E1.0"),sQuery(id+"F0.wireOp",EDGE,"E1.1"),sQuery(id+"F0.wireOp",EDGE,"E1.2"),sQuery(id+"F0.wireOp",EDGE,"E1.3"),sQuery(id+"F0.wireOp",EDGE,"E1.4"),sQuery(id+"F0.wireOp",EDGE,"E1.5"),sQuery(id+"F0.wireOp",EDGE,"E2"),sQuery(id+"F0.wireOp",EDGE,"E3"),sQuery(id+"F0.wireOp",EDGE,"E4"),sQuery(id+"F0.wireOp",EDGE,"E5"),sQuery(id+"F0.wireOp",EDGE,"E6"),sQuery(id+"F0.wireOp",EDGE,"E7"),sQuery(id+"F0.wireOp",EDGE,"E8.filletArc"),sQuery(id+"F0.wireOp",EDGE,"E9.filletArc"),sQuery(id+"F0.wireOp",EDGE,"E10.filletArc"),sQuery(id+"F0.wireOp",EDGE,"E11.filletArc"),sQuery(id+"F0.wireOp",EDGE,"E12.filletArc"),sQuery(id+"F0.wireOp",EDGE,"E13.filletArc"),sQuery(id+"F0.wireOp",EDGE,"E14.filletArc"),sQuery(id+"F0.wireOp",EDGE,"E15.filletArc"),sQuery(id+"F0.wireOp",EDGE,"E16.filletArc"),sQuery(id+"F0.wireOp",EDGE,"E17"),sQuery(id+"F0.wireOp",EDGE,"E18"),sQuery(id+"F0.wireOp",EDGE,"E19"),sQuery(id+"F0.wireOp",EDGE,"E20.filletArc"),sQuery(id+"F0.wireOp",EDGE,"E21.filletArc"),sQuery(id+"F0.wireOp",EDGE,"E22.filletArc"),sQuery(id+"F0.wireOp",EDGE,"E23.filletArc"),sQuery(id+"F0.wireOp",EDGE,"E24.filletArc"),sQuery(id+"F0.wireOp",EDGE,"E25.filletArc")])]});
            hole(context, id + "F20", {"style" : HoleStyle.SIMPLE, "endStyle" : HoleEndStyle.BLIND, "holeDiameter" : 6 * mm, "holeDepth" : 2 * mm, "tappedDepth" : 12 * mm, "tapClearance" : 3, "locations" : qUnion([Q0, Q1]), "scope" : qUnion([Q2])});
        }
        {
            var Q0;
            Q0=sQuery(id+"F0.wireOp",VERTEX,"E1.cCircle.center");
            var Q1;
            Q1=makeQuery(id+"F1.opExtrude","SWEPT_BODY",BODY,{"disambiguationData":[OSD([sQuery(id+"F0.wireOp",EDGE,"E0.0"),sQuery(id+"F0.wireOp",EDGE,"E0.1"),sQuery(id+"F0.wireOp",EDGE,"E0.2"),sQuery(id+"F0.wireOp",EDGE,"E0.3"),sQuery(id+"F0.wireOp",EDGE,"E0.4"),sQuery(id+"F0.wireOp",EDGE,"E0.5"),sQuery(id+"F0.wireOp",EDGE,"E1.0"),sQuery(id+"F0.wireOp",EDGE,"E1.1"),sQuery(id+"F0.wireOp",EDGE,"E1.2"),sQuery(id+"F0.wireOp",EDGE,"E1.3"),sQuery(id+"F0.wireOp",EDGE,"E1.4"),sQuery(id+"F0.wireOp",EDGE,"E1.5"),sQuery(id+"F0.wireOp",EDGE,"E2"),sQuery(id+"F0.wireOp",EDGE,"E3"),sQuery(id+"F0.wireOp",EDGE,"E4"),sQuery(id+"F0.wireOp",EDGE,"E5"),sQuery(id+"F0.wireOp",EDGE,"E6"),sQuery(id+"F0.wireOp",EDGE,"E7"),sQuery(id+"F0.wireOp",EDGE,"E8.filletArc"),sQuery(id+"F0.wireOp",EDGE,"E9.filletArc"),sQuery(id+"F0.wireOp",EDGE,"E10.filletArc"),sQuery(id+"F0.wireOp",EDGE,"E11.filletArc"),sQuery(id+"F0.wireOp",EDGE,"E12.filletArc"),sQuery(id+"F0.wireOp",EDGE,"E13.filletArc"),sQuery(id+"F0.wireOp",EDGE,"E14.filletArc"),sQuery(id+"F0.wireOp",EDGE,"E15.filletArc"),sQuery(id+"F0.wireOp",EDGE,"E16.filletArc"),sQuery(id+"F0.wireOp",EDGE,"E17"),sQuery(id+"F0.wireOp",EDGE,"E18"),sQuery(id+"F0.wireOp",EDGE,"E19"),sQuery(id+"F0.wireOp",EDGE,"E20.filletArc"),sQuery(id+"F0.wireOp",EDGE,"E21.filletArc"),sQuery(id+"F0.wireOp",EDGE,"E22.filletArc"),sQuery(id+"F0.wireOp",EDGE,"E23.filletArc"),sQuery(id+"F0.wireOp",EDGE,"E24.filletArc"),sQuery(id+"F0.wireOp",EDGE,"E25.filletArc")])]});
            hole(context, id + "F21", {"style" : HoleStyle.SIMPLE, "endStyle" : HoleEndStyle.BLIND, "oppositeDirection" : true, "standardTappedOrClearance" : lookupTablePath({ "standard" : "ANSI", "engagement" : "75%", "pitch" : "20 tpi", "size" : "1/4", "type" : "Tapped" }), "standardBlindInLast" : lookupTablePath({ "standard" : "ANSI", "engagement" : "75%", "pitch" : "20 tpi", "size" : "1/4", "type" : "Tapped" }), "holeDiameter" : 5.1 * mm, "showTappedDepth" : true, "holeDepth" : 15.8 * mm, "tappedDepth" : 12 * mm, "tapClearance" : 3, "locations" : qUnion([Q0]), "scope" : qUnion([Q1]), "majorDiameter" : 6.35 * mm});
        }
    });
